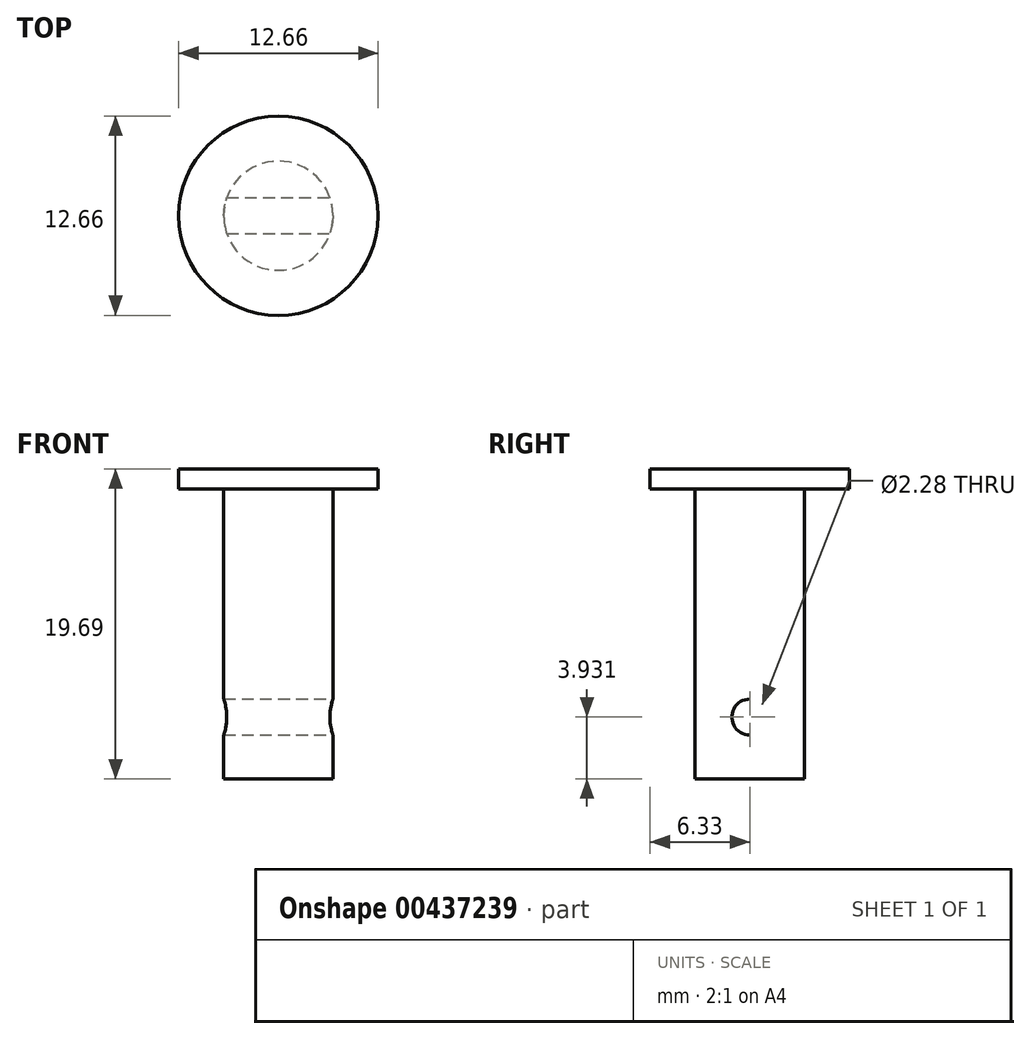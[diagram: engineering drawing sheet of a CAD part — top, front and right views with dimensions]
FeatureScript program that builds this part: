
annotation { "Feature Type Name" : "Feature", "Feature Type Description" : "" }
export const myFeature = defineFeature(function(context is Context, id is Id, definition is map)
    precondition{}
    {
        {
            var Q0;
            Q0=qCreatedBy(makeId("Top.planeOp"),FACE);
            var sketch = newSketch(context, id + "F0", { "sketchPlane" : qUnion([Q0])});
            skCircle(sketch, "E0", {"center": v(0, 0) * mm, "radius": 3.47 * mm});
            skSolve(sketch);
        }
        {
            var Q0;
            Q0=makeQuery(id+"F0.imprint","IMPRINT",FACE,{"disambiguationData":[TD([[makeQuery(id+"F0.imprint","IMPRINT",EDGE,{"derivedFrom":sQuery(id+"F0.wireOp",EDGE,"E0")}),1.0]])]});
            var Q1;
            Q1=sQuery(id+"F0.wireOp",EDGE,"E0");
            extrude(context, id + "F1", {"entities" : qUnion([Q0]), "surfaceEntities" : qUnion([Q1]), "endBound" : BoundingType.SYMMETRIC, "depth" : 19.05 * mm});
        }
        {
            var Q0;
            Q0=makeQuery(id+"F1.opExtrude","CAP_FACE",FACE,{"disambiguationData":[OSD([sQuery(id+"F0.wireOp",EDGE,"E0")])],"isStart":false});
            var sketch = newSketch(context, id + "F2", { "sketchPlane" : qUnion([Q0])});
            skCircle(sketch, "E1", {"center": v(0, 0) * mm, "radius": 6.33 * mm});
            skSolve(sketch);
        }
        {
            var Q0;
            Q0 = qSketchRegion(id + "F2", true);
            extrude(context, id + "F3", {"entities" : qUnion([Q0]), "operationType" : NewBodyOperationType.ADD, "endBound" : BoundingType.SYMMETRIC, "depth" : 1.27 * mm});
        }
        {
            var Q0;
            Q0=qCreatedBy(makeId("Right.planeOp"),FACE);
            var sketch = newSketch(context, id + "F4", { "sketchPlane" : qUnion([Q0])});
            skCircle(sketch, "E2", {"center": v(0, -5.6) * mm, "radius": 1.14 * mm});
            skSolve(sketch);
        }
        {
            var Q0;
            Q0 = qSketchRegion(id + "F4", true);
            extrude(context, id + "F5", {"entities" : qUnion([Q0]), "operationType" : NewBodyOperationType.REMOVE, "endBound" : BoundingType.SYMMETRIC, "oppositeDirection" : true, "depth" : 25.4 * mm});
        }
    });
